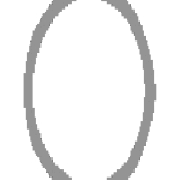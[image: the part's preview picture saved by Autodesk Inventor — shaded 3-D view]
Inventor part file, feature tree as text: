
AUTODESK INVENTOR PART (.ipt)
format: ipt  version: 2021 (Build 250183000, 183)  size: 143,360 bytes
history: native  units: in
note: dims shown in document units (in); Inventor stores cm internally (conversion verified against a paired STEP export)
features: plane x7, sketch x5, other x4, extrude x2, boolean_combine x2
ambient origin geometry x8: Origin, YZ Plane, XZ Plane, XY Plane, X Axis, Y Axis, Z Axis, Center Point
bodies: Solid1 (feature_tree), Body (feature_tree), Solid2 (feature_tree), Solid3 (feature_tree)
feature tree (20):
  other  "Driven Length"
  other  "Frame Generator"
  other  "Start Plane"
  other  "End Plane"
  plane  "Work Plane4"
  plane  "Work Plane5"
  plane  "Work Plane6"
  extrude  "Extrusion3"  Depth=0.065in
  boolean_combine  "Combine1"
  plane  "Work Plane7"
  plane  "Work Plane8"
  plane  "Work Plane9"
  extrude  "Extrusion4"  TaperAngle=0.0deg  [1 undecoded]
  boolean_combine  "Combine2"
  sketch  "Sketch"  dims[d8=90.0deg d9=12.431in d10=0.12in d11=0.0in d12=0.12in d13=0.0in]
  sketch  "Sketch2"  dims[d0=1.0in d1=0.065in]
  plane  "Work Plane3"
  sketch  "Sketch3"  dims[d2=12.431in d4=-0.0in]
  sketch  "Sketch4"  dims[d5=12.431in]
  sketch  "Sketch5"  dims[d6=0.12in d7=0.0in]
note: 1 required parameter value undecoded (feature->parameter linkage not recoverable at this tier; creation-order binding heuristic only, values carry confidence <= 0.55)
